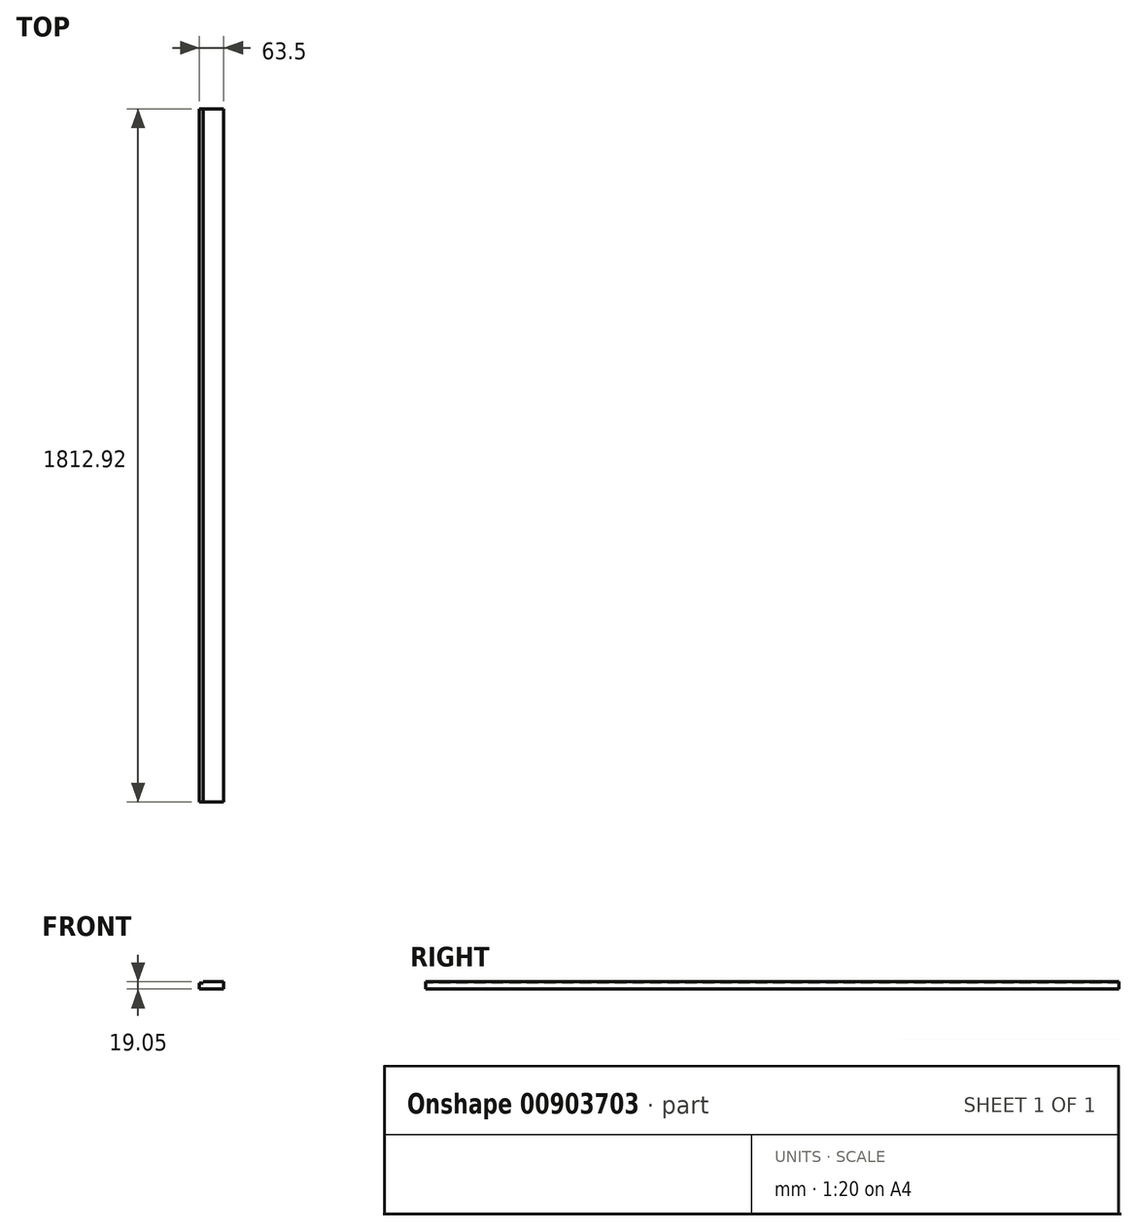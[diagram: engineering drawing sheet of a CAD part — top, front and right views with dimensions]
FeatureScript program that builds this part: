
annotation { "Feature Type Name" : "Feature", "Feature Type Description" : "" }
export const myFeature = defineFeature(function(context is Context, id is Id, definition is map)
    precondition{}
    {
        {
            var Q0;
            Q0=qCreatedBy(makeId("Top.planeOp"),FACE);
            var sketch = newSketch(context, id + "F0", { "sketchPlane" : qUnion([Q0])});
            skLineSegment(sketch, "E0.bottom", {"start": v(0, -906.46) * mm, "end": v(-63.5, -906.46) * mm});
            skLineSegment(sketch, "E0.top", {"start": v(0, 906.46) * mm, "end": v(-63.5, 906.46) * mm});
            skLineSegment(sketch, "E0.left", {"start": v(0, -906.46) * mm, "end": v(0, 906.46) * mm});
            skLineSegment(sketch, "E0.right", {"start": v(-63.5, -906.46) * mm, "end": v(-63.5, 906.46) * mm});
            skSolve(sketch);
        }
        {
            var Q0;
            Q0=makeQuery(id+"F0.imprint","IMPRINT",FACE,{"disambiguationData":[TD([[makeQuery(id+"F0.imprint","IMPRINT",EDGE,{"derivedFrom":sQuery(id+"F0.wireOp",EDGE,"E0.bottom")}),-1.0]])]});
            extrude(context, id + "F1", {"entities" : qUnion([Q0]), "depth" : 19.05 * mm, "offsetDistance" : 25 * mm});
        }
        {
            var Q0;
            Q0=makeQuery(id+"F1.opExtrude","SWEPT_FACE",FACE,{"disambiguationData":[OSD([sQuery(id+"F0.wireOp",EDGE,"E0.bottom")])]});
            var sketch = newSketch(context, id + "F2", { "sketchPlane" : qUnion([Q0])});
            skLineSegment(sketch, "E1.top", {"start": v(-63.5, 15.88) * mm, "end": v(-53.97, 15.88) * mm});
            skLineSegment(sketch, "E1.right", {"start": v(-53.97, 19.05) * mm, "end": v(-53.97, 15.88) * mm});
            skSolve(sketch);
        }
        {
            var Q0;
            {var subQ0=sQuery(id+"F2.wireOp",EDGE,"E1.top");Q0=makeQuery(id+"F2.imprint","IMPRINT",FACE,{"disambiguationData":[TD([[makeQuery(id+"F2.imprint","IMPRINT",EDGE,{"derivedFrom":subQ0}),1.0]])]});}
            extrude(context, id + "F3", {"entities" : qUnion([Q0]), "operationType" : NewBodyOperationType.REMOVE, "endBound" : BoundingType.THROUGH_ALL, "oppositeDirection" : true, "depth" : 25 * mm, "offsetDistance" : 25 * mm});
        }
    });
